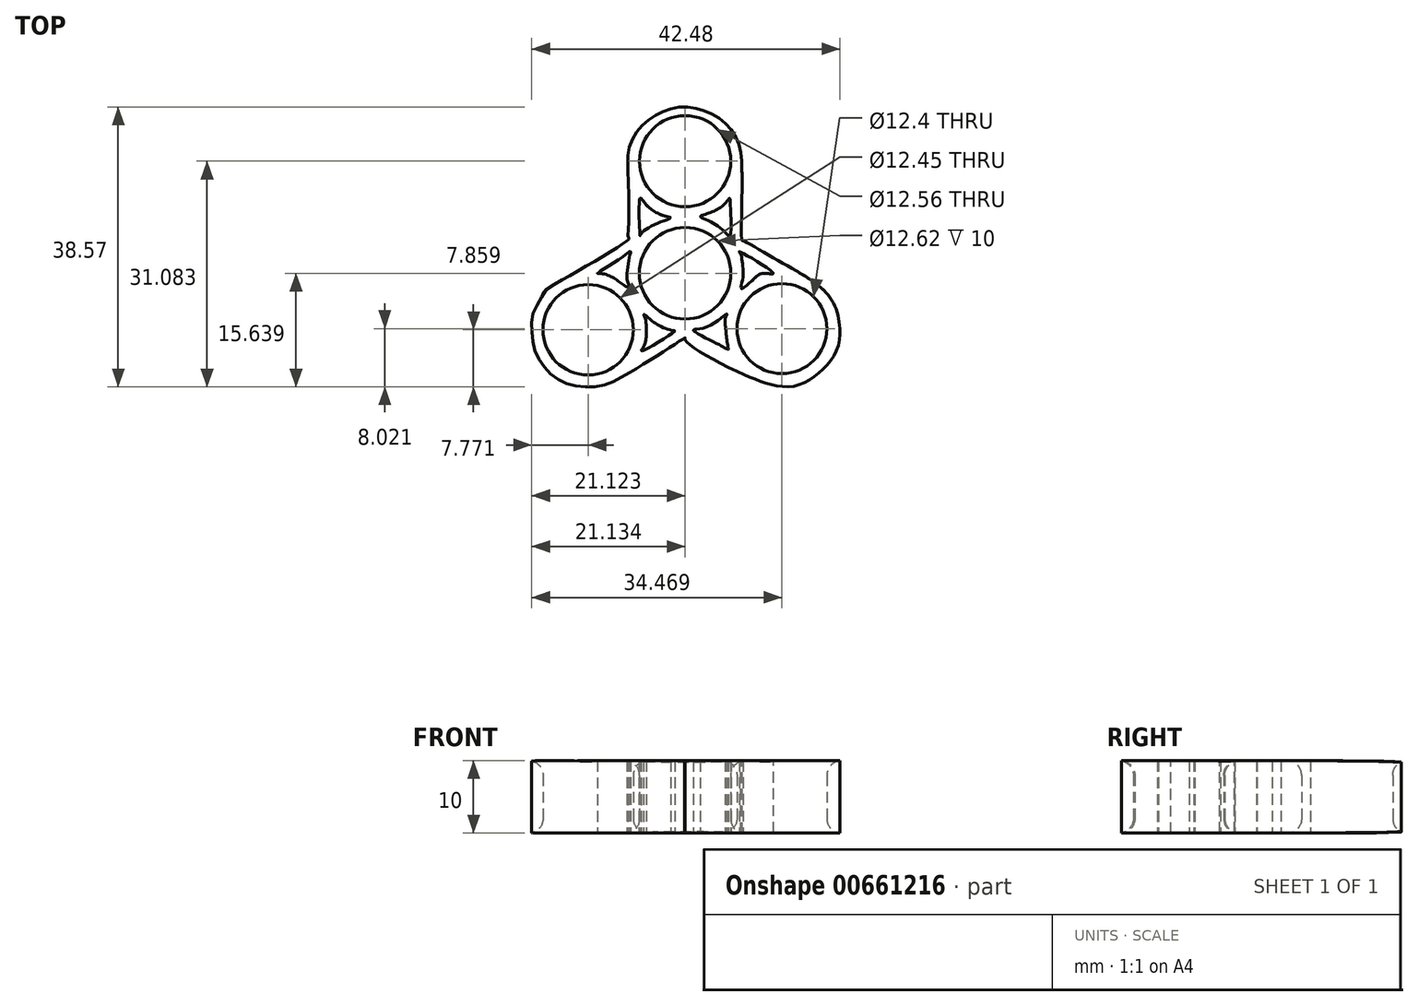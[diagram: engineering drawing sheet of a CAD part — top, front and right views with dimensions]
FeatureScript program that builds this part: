
annotation { "Feature Type Name" : "Feature", "Feature Type Description" : "" }
export const myFeature = defineFeature(function(context is Context, id is Id, definition is map)
    precondition{}
    {
        {
            var Q0;
            Q0=qCreatedBy(makeId("Top.planeOp"),FACE);
            var sketch = newSketch(context, id + "F0", { "sketchPlane" : qUnion([Q0])});
            skCircle(sketch, "E0", {"center": v(-17.88, 8.24) * mm, "radius": 6.3 * mm});
            skPoint(sketch, "E0.first.point", {"position": v(-23.67, 5.75) * mm});
            skPoint(sketch, "E0.second.point", {"position": v(-12.32, 11.22) * mm});
            skPoint(sketch, "E0.third.point", {"position": v(-11.97, 10.47) * mm});
            skCircle(sketch, "E1", {"center": v(-17.87, 23.68) * mm, "radius": 6.28 * mm});
            skPoint(sketch, "E1.first.point", {"position": v(-23.13, 20.25) * mm});
            skPoint(sketch, "E1.second.point", {"position": v(-12.6, 27.1) * mm});
            skPoint(sketch, "E1.third.point", {"position": v(-11.97, 25.86) * mm});
            skCircle(sketch, "E2", {"center": v(-31.23, 0.46) * mm, "radius": 6.22 * mm});
            skPoint(sketch, "E2.first.point", {"position": v(-36.4, -3) * mm});
            skPoint(sketch, "E2.second.point", {"position": v(-26.34, 4.31) * mm});
            skPoint(sketch, "E2.third.point", {"position": v(-25.8, 3.49) * mm});
            skCircle(sketch, "E3", {"center": v(-4.53, 0.62) * mm, "radius": 6.2 * mm});
            skPoint(sketch, "E3.first.point", {"position": v(-10.33, 2.8) * mm});
            skPoint(sketch, "E3.second.point", {"position": v(1.36, -1.3) * mm});
            skPoint(sketch, "E3.third.point", {"position": v(1.64, 0) * mm});
            skFitSpline(sketch, "E4", {"points": [v(-25.66, 12.93) * mm, v(-36.88, 6.09) * mm, v(-37.42, 5.47) * mm, v(-38.24, 3.83) * mm, v(-38.8, 2.94) * mm, v(-39, 1.37) * mm, v(-38.93, 0) * mm, v(-38.65, -2.12) * mm, v(-37.5, -4.38) * mm, v(-34.82, -6.7) * mm, v(-30.51, -7.39) * mm, v(-26.61, -6.09) * mm, v(-17.86, -0.61) * mm, v(-17.93, -0.82) * mm, v(-6.64, -6.9) * mm, v(-1.65, -6.9) * mm, v(0.95, -5.13) * mm, v(3.21, -1.85) * mm, v(3.28, 1.92) * mm, v(2.05, 5) * mm, v(-1.17, 7.73) * mm, v(-6.37, 10.74) * mm, v(-9.92, 12.72) * mm, v(-10.06, 12.8) * mm, v(-10.13, 24.01) * mm, v(-11.45, 27.91) * mm, v(-13.64, 29.9) * mm, v(-16.24, 30.92) * mm, v(-18.77, 31.13) * mm, v(-21.65, 30.17) * mm, v(-24.1, 28.25) * mm, v(-25.61, 25.31) * mm, v(-25.68, 20.73) * mm, v(-25.68, 14.37) * mm, v(-25.69, 13.21) * mm, v(-25.66, 12.93) * mm]});
            skFitSpline(sketch, "E5", {"points": [v(-23.85, -2.44) * mm, v(-19.28, 0.27) * mm, v(-19.35, 0.32) * mm, v(-20.44, 0.58) * mm, v(-21.6, 1.14) * mm, v(-22.74, 1.94) * mm, v(-23.56, 2.6) * mm, v(-23.58, 2.54) * mm, v(-23.34, 1.99) * mm, v(-23.24, 0.8) * mm, v(-23.24, -0.63) * mm, v(-23.66, -2) * mm, v(-23.85, -2.44) * mm]});
            skFitSpline(sketch, "E6", {"points": [v(-16.71, 0.39) * mm, v(-14.85, 0.85) * mm, v(-12.12, 2.66) * mm, v(-12.14, 2.52) * mm, v(-12.32, 2.01) * mm, v(-12.32, 0.97) * mm, v(-11.93, -2.13) * mm, v(-11.9, -2.32) * mm, v(-12.32, -2.08) * mm, v(-13.57, -1.4) * mm, v(-16.71, 0.39) * mm]});
            skFitSpline(sketch, "E7", {"points": [v(-10.16, 6.13) * mm, v(-8.51, 7.36) * mm, v(-7.04, 8.24) * mm, v(-5.7, 8.24) * mm, v(-10.4, 11.22) * mm, v(-10.26, 10.95) * mm, v(-9.98, 9.65) * mm, v(-9.95, 7.4) * mm, v(-10.16, 6.13) * mm]});
            skFitSpline(sketch, "E8", {"points": [v(-25.55, 6.3) * mm, v(-25.8, 7.02) * mm, v(-25.8, 8.86) * mm, v(-25.48, 10.74) * mm, v(-25.38, 11.22) * mm, v(-25.51, 11.22) * mm, v(-26.37, 10.6) * mm, v(-29.96, 8.24) * mm, v(-29.86, 8.24) * mm, v(-28.18, 7.84) * mm, v(-25.95, 6.39) * mm, v(-25.55, 6.3) * mm]});
            skFitSpline(sketch, "E9", {"points": [v(-24.08, 18.55) * mm, v(-24.08, 13.39) * mm, v(-24.05, 13.52) * mm, v(-22, 15) * mm, v(-19.84, 15.89) * mm, v(-20.01, 15.95) * mm, v(-21.31, 16.36) * mm, v(-23.36, 17.83) * mm, v(-24.08, 18.55) * mm]});
            skFitSpline(sketch, "E10", {"points": [v(-15.77, 16.06) * mm, v(-13.07, 17.25) * mm, v(-11.73, 18.62) * mm, v(-11.7, 18.55) * mm, v(-11.67, 13.39) * mm, v(-11.84, 13.39) * mm, v(-12.7, 14.2) * mm, v(-14.88, 15.61) * mm, v(-15.77, 16.06) * mm]});
            skSolve(sketch);
        }
        {
            var Q0;
            Q0=makeQuery(id+"F0.imprint","IMPRINT",FACE,{"disambiguationData":[TD([[makeQuery(id+"F0.imprint","IMPRINT",EDGE,{"derivedFrom":sQuery(id+"F0.wireOp",EDGE,"E0")}),-1.0]])]});
            extrude(context, id + "F1", {"entities" : qUnion([Q0]), "depth" : 10 * mm, "offsetDistance" : 25 * mm});
        }
        {
            var Q0;
            Q0=makeQuery(id+"F1.opExtrude","CAP_EDGE",EDGE,{"disambiguationData":[OSD([sQuery(id+"F0.wireOp",EDGE,"E1")])],"isStart":false});
            var Q1;
            Q1=makeQuery(id+"F1.opExtrude","CAP_EDGE",EDGE,{"disambiguationData":[OSD([sQuery(id+"F0.wireOp",EDGE,"E2")])],"isStart":false});
            var Q2;
            Q2=makeQuery(id+"F1.opExtrude","CAP_EDGE",EDGE,{"disambiguationData":[OSD([sQuery(id+"F0.wireOp",EDGE,"E3")])],"isStart":false});
            var Q3;
            Q3=makeQuery(id+"F1.opExtrude","CAP_EDGE",EDGE,{"disambiguationData":[OSD([sQuery(id+"F0.wireOp",EDGE,"E3")])],"isStart":true});
            var Q4;
            Q4=makeQuery(id+"F1.opExtrude","CAP_EDGE",EDGE,{"disambiguationData":[OSD([sQuery(id+"F0.wireOp",EDGE,"E2")])],"isStart":true});
            var Q5;
            Q5=makeQuery(id+"F1.opExtrude","CAP_EDGE",EDGE,{"disambiguationData":[OSD([sQuery(id+"F0.wireOp",EDGE,"E1")])],"isStart":true});
            fillet(context, id + "F2", {"entities" : qUnion([Q0, Q1, Q2, Q3, Q4, Q5]), "radius" : 2 * mm, "tangentPropagation" : true, "allowEdgeOverflow" : false});
        }
    });
